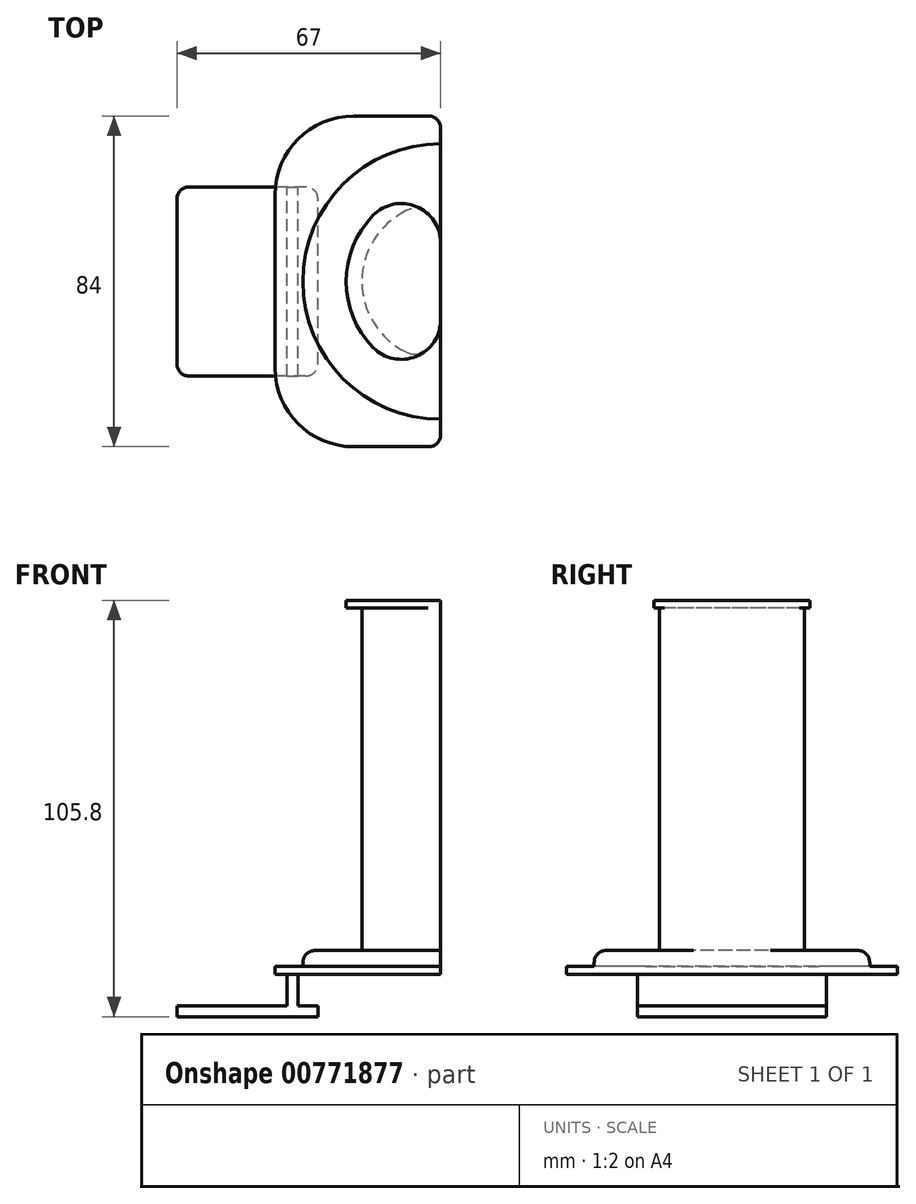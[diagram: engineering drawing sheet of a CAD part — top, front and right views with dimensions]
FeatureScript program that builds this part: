
annotation { "Feature Type Name" : "Feature", "Feature Type Description" : "" }
export const myFeature = defineFeature(function(context is Context, id is Id, definition is map)
    precondition{}
    {
        {
            var Q0;
            Q0=qCreatedBy(makeId("Top.planeOp"),FACE);
            var sketch = newSketch(context, id + "F0", { "sketchPlane" : qUnion([Q0])});
            skCircle(sketch, "E0", {"center": v(0, 0) * mm, "radius": 42 * mm});
            skCircle(sketch, "E1", {"center": v(0, 0) * mm, "radius": 35 * mm});
            skCircle(sketch, "E2", {"center": v(0, 0) * mm, "radius": 20 * mm});
            skLineSegment(sketch, "E3", {"start": v(0, -20) * mm, "end": v(0, 20) * mm});
            skLineSegment(sketch, "E4", {"start": v(0, -42) * mm, "end": v(0, 42) * mm});
            skLineSegment(sketch, "E5.bottom", {"start": v(-22.08, -42) * mm, "end": v(22.08, -42) * mm});
            skLineSegment(sketch, "E5.top", {"start": v(-22.08, 42) * mm, "end": v(22.08, 42) * mm});
            skLineSegment(sketch, "E5.left", {"start": v(-42.08, -22) * mm, "end": v(-42.08, 22) * mm});
            skLineSegment(sketch, "E5.right", {"start": v(42.08, -22) * mm, "end": v(42.08, 22) * mm});
            skPoint(sketch, "E6.visualSharp", {"position": v(-42.08, -42) * mm});
            skArc(sketch, "E6.filletArc", {"start": v(-42.08, -22) * mm, "mid": v(-36.23, -36.14) * mm, "end": v(-22.08, -42) * mm});
            skPoint(sketch, "E7.visualSharp", {"position": v(-42.08, 42) * mm});
            skArc(sketch, "E7.filletArc", {"start": v(-22.08, 42) * mm, "mid": v(-36.23, 36.14) * mm, "end": v(-42.08, 22) * mm});
            skPoint(sketch, "E8.visualSharp", {"position": v(42.08, -42) * mm});
            skArc(sketch, "E8.filletArc", {"start": v(22.08, -42) * mm, "mid": v(36.23, -36.14) * mm, "end": v(42.08, -22) * mm});
            skPoint(sketch, "E9.visualSharp", {"position": v(42.08, 42) * mm});
            skArc(sketch, "E9.filletArc", {"start": v(42.08, 22) * mm, "mid": v(36.23, 36.14) * mm, "end": v(22.08, 42) * mm});
            skSolve(sketch);
        }
        {
            var Q0;
            {var subQ0=sQuery(id+"F0.wireOp",EDGE,"E4");var subQ4=sQuery(id+"F0.wireOp",EDGE,"E1");var subQ6=makeQuery(id+"F0.imprint","INTERSECT",VERTEX,{"disambiguationData":[OD(0.0)],"derivedFrom":[subQ4,subQ0]});Q0=makeQuery(id+"F0.imprint","IMPRINT",FACE,{"disambiguationData":[TD([[makeQuery(id+"F0.imprint","IMPRINT",EDGE,{"disambiguationData":[TD([[subQ6,1.0]])],"derivedFrom":subQ4}),-1.0]])]});}
            var Q1;
            {var subQ0=sQuery(id+"F0.wireOp",EDGE,"E4");var subQ1=sQuery(id+"F0.wireOp",EDGE,"E2");var subQ2=makeQuery(id+"F0.imprint","INTERSECT",VERTEX,{"disambiguationData":[OD(0.0)],"derivedFrom":[subQ1,subQ0]});Q1=makeQuery(id+"F0.imprint","IMPRINT",FACE,{"disambiguationData":[TD([[makeQuery(id+"F0.imprint","IMPRINT",EDGE,{"disambiguationData":[TD([[subQ2,1.0]])],"derivedFrom":subQ1}),1.0]])]});}
            var Q2;
            {var subQ0=sQuery(id+"F0.wireOp",EDGE,"E4");var subQ1=sQuery(id+"F0.wireOp",EDGE,"E1");var subQ2=makeQuery(id+"F0.imprint","INTERSECT",VERTEX,{"disambiguationData":[OD(0.0)],"derivedFrom":[subQ1,subQ0]});Q2=makeQuery(id+"F0.imprint","IMPRINT",FACE,{"disambiguationData":[TD([[makeQuery(id+"F0.imprint","IMPRINT",EDGE,{"disambiguationData":[TD([[subQ2,1.0]])],"derivedFrom":subQ1}),1.0]])]});}
            var Q3;
            Q3=makeQuery(id+"F0.imprint","IMPRINT",FACE,{"disambiguationData":[TD([[makeQuery(id+"F0.imprint","IMPRINT",EDGE,{"derivedFrom":sQuery(id+"F0.wireOp",EDGE,"E5.left")}),-1.0]])]});
            extrude(context, id + "F1", {"entities" : qUnion([Q0, Q1, Q2, Q3]), "depth" : 2 * mm});
        }
        {
            var Q0;
            {var subQ0=sQuery(id+"F0.wireOp",EDGE,"E4");var subQ1=sQuery(id+"F0.wireOp",EDGE,"E1");var subQ2=makeQuery(id+"F0.imprint","INTERSECT",VERTEX,{"disambiguationData":[OD(0.0)],"derivedFrom":[subQ1,subQ0]});Q0=makeQuery(id+"F0.imprint","IMPRINT",FACE,{"disambiguationData":[TD([[makeQuery(id+"F0.imprint","IMPRINT",EDGE,{"disambiguationData":[TD([[subQ2,1.0]])],"derivedFrom":subQ1}),1.0]])]});}
            var Q1;
            {var subQ0=sQuery(id+"F0.wireOp",EDGE,"E4");var subQ1=sQuery(id+"F0.wireOp",EDGE,"E2");var subQ2=makeQuery(id+"F0.imprint","INTERSECT",VERTEX,{"disambiguationData":[OD(0.0)],"derivedFrom":[subQ1,subQ0]});Q1=makeQuery(id+"F0.imprint","IMPRINT",FACE,{"disambiguationData":[TD([[makeQuery(id+"F0.imprint","IMPRINT",EDGE,{"disambiguationData":[TD([[subQ2,1.0]])],"derivedFrom":subQ1}),1.0]])]});}
            extrude(context, id + "F2", {"entities" : qUnion([Q0, Q1]), "operationType" : NewBodyOperationType.ADD, "depth" : 6 * mm});
        }
        {
            var Q0;
            {var subQ0=sQuery(id+"F0.wireOp",EDGE,"E4");var subQ1=sQuery(id+"F0.wireOp",EDGE,"E2");var subQ2=makeQuery(id+"F0.imprint","INTERSECT",VERTEX,{"disambiguationData":[OD(0.0)],"derivedFrom":[subQ1,subQ0]});Q0=makeQuery(id+"F0.imprint","IMPRINT",FACE,{"disambiguationData":[TD([[makeQuery(id+"F0.imprint","IMPRINT",EDGE,{"disambiguationData":[TD([[subQ2,1.0]])],"derivedFrom":subQ1}),1.0]])]});}
            extrude(context, id + "F3", {"entities" : qUnion([Q0]), "operationType" : NewBodyOperationType.ADD, "depth" : 95 * mm, "offsetDistance" : 25 * mm});
        }
        {
            var Q0;
            Q0=makeQuery(id+"F3.opExtrude","CAP_FACE",FACE,{"disambiguationData":[OSD([sQuery(id+"F0.wireOp",EDGE,"E2")])],"isStart":false});
            var sketch = newSketch(context, id + "F4", { "sketchPlane" : qUnion([Q0])});
            skCircle(sketch, "E10", {"center": v(0, 0) * mm, "radius": 24 * mm});
            skLineSegment(sketch, "E11", {"start": v(0, 24) * mm, "end": v(0, -24) * mm});
            skSolve(sketch);
        }
        {
            var Q0;
            {var subQ0=sQuery(id+"F4.wireOp",EDGE,"E11");var subQ1=sQuery(id+"F4.wireOp",EDGE,"E10");var subQ2=makeQuery(id+"F4.imprint","INTERSECT",VERTEX,{"disambiguationData":[OD(0.0)],"derivedFrom":[subQ1,subQ0]});Q0=makeQuery(id+"F4.imprint","IMPRINT",FACE,{"disambiguationData":[TD([[makeQuery(id+"F4.imprint","IMPRINT",EDGE,{"disambiguationData":[TD([[subQ2,-1.0]])],"derivedFrom":subQ1}),1.0]])]});}
            extrude(context, id + "F5", {"entities" : qUnion([Q0]), "operationType" : NewBodyOperationType.ADD, "oppositeDirection" : true, "depth" : 2 * mm});
        }
        {
            var Q0;
            {var subQ0=sQuery(id+"F4.wireOp",EDGE,"E11");var subQ1=sQuery(id+"F4.wireOp",EDGE,"E10");Q0=makeQuery(id+"F5.opExtrude","SWEPT_EDGE",EDGE,{"disambiguationData":[OSD([subQ1,subQ0]),TDD([makeQuery(id+"F4.imprint","INTERSECT",VERTEX,{"disambiguationData":[OD(0.0)],"derivedFrom":[subQ1,subQ0]})])]});}
            var Q1;
            {var subQ0=sQuery(id+"F4.wireOp",EDGE,"E11");var subQ1=sQuery(id+"F4.wireOp",EDGE,"E10");Q1=makeQuery(id+"F5.opExtrude","SWEPT_EDGE",EDGE,{"disambiguationData":[OSD([subQ1,subQ0]),TDD([makeQuery(id+"F4.imprint","INTERSECT",VERTEX,{"disambiguationData":[OD(1.0)],"derivedFrom":[subQ1,subQ0]})])]});}
            fillet(context, id + "F6", {"entities" : qUnion([Q0, Q1]), "radius" : 10 * mm, "tangentPropagation" : true, "allowEdgeOverflow" : false});
        }
        {
            var Q0;
            {var subQ0=sQuery(id+"F0.wireOp",EDGE,"E4");var subQ1=sQuery(id+"F0.wireOp",EDGE,"E1");var subQ2=makeQuery(id+"F0.imprint","INTERSECT",VERTEX,{"disambiguationData":[OD(0.0)],"derivedFrom":[subQ1,subQ0]});Q0=makeQuery(id+"F0.imprint","IMPRINT",FACE,{"disambiguationData":[TD([[makeQuery(id+"F0.imprint","IMPRINT",EDGE,{"disambiguationData":[TD([[subQ2,1.0]])],"derivedFrom":subQ1}),1.0]])]});}
            var sketch = newSketch(context, id + "F7", { "sketchPlane" : qUnion([Q0])});
            skLineSegment(sketch, "E12.bottom", {"start": v(-39, -24) * mm, "end": v(-36.2, -24) * mm});
            skLineSegment(sketch, "E12.top", {"start": v(-39, 24) * mm, "end": v(-36.2, 24) * mm});
            skLineSegment(sketch, "E12.left", {"start": v(-39, -24) * mm, "end": v(-39, 24) * mm});
            skLineSegment(sketch, "E12.right", {"start": v(-36.2, -24) * mm, "end": v(-36.2, 24) * mm});
            skPoint(sketch, "E12.middle", {"position": v(-37.6, 0) * mm});
            skSolve(sketch);
        }
        {
            var Q0;
            Q0=makeQuery(id+"F7.imprint","IMPRINT",FACE,{"disambiguationData":[TD([[makeQuery(id+"F7.imprint","IMPRINT",EDGE,{"derivedFrom":sQuery(id+"F7.wireOp",EDGE,"E12.bottom")}),1.0]])]});
            extrude(context, id + "F8", {"entities" : qUnion([Q0]), "operationType" : NewBodyOperationType.ADD, "oppositeDirection" : true, "depth" : 8 * mm});
        }
        {
            var Q0;
            Q0=makeQuery(id+"F8.opExtrude","CAP_FACE",FACE,{"disambiguationData":[OSD([sQuery(id+"F7.wireOp",EDGE,"E12.bottom"),sQuery(id+"F7.wireOp",EDGE,"E12.top"),sQuery(id+"F7.wireOp",EDGE,"E12.left"),sQuery(id+"F7.wireOp",EDGE,"E12.right")])],"isStart":false});
            var sketch = newSketch(context, id + "F9", { "sketchPlane" : qUnion([Q0])});
            skLineSegment(sketch, "E13.bottom", {"start": v(-11, 24) * mm, "end": v(-67, 24) * mm});
            skLineSegment(sketch, "E13.top", {"start": v(-11, -24) * mm, "end": v(-67, -24) * mm});
            skLineSegment(sketch, "E13.left", {"start": v(-11, 24) * mm, "end": v(-11, -24) * mm});
            skLineSegment(sketch, "E13.right", {"start": v(-67, 24) * mm, "end": v(-67, -24) * mm});
            skPoint(sketch, "E13.middle", {"position": v(-39, 0) * mm});
            skLineSegment(sketch, "E14", {"start": v(-31.2, 24) * mm, "end": v(-31.2, -24) * mm});
            skSolve(sketch);
        }
        {
            var Q0;
            {var subQ2=sQuery(id+"F9.wireOp",EDGE,"E13.right");Q0=makeQuery(id+"F9.imprint","IMPRINT",FACE,{"disambiguationData":[TD([[makeQuery(id+"F9.imprint","IMPRINT",EDGE,{"derivedFrom":subQ2}),1.0]])]});}
            var Q1;
            {var subQ2=sQuery(id+"F9.wireOp",EDGE,"E14");Q1=makeQuery(id+"F9.imprint","IMPRINT",FACE,{"disambiguationData":[TD([[makeQuery(id+"F9.imprint","IMPRINT",EDGE,{"derivedFrom":subQ2}),-1.0]])]});}
            var Q2;
            {var subQ1=makeQuery(id+"F8.opExtrude","CAP_EDGE",EDGE,{"disambiguationData":[OSD([sQuery(id+"F7.wireOp",EDGE,"E12.left")])],"isStart":false});Q2=makeQuery(id+"F9.imprint","IMPRINT",FACE,{"disambiguationData":[TD([[makeQuery(id+"F9.imprint","IMPRINT",EDGE,{"derivedFrom":subQ1}),1.0]])]});}
            extrude(context, id + "F10", {"entities" : qUnion([Q0, Q1, Q2]), "operationType" : NewBodyOperationType.ADD, "depth" : 2.8 * mm});
        }
        {
            var Q0;
            Q0=makeQuery(id+"F10.opExtrude","SWEPT_EDGE",EDGE,{"disambiguationData":[OSD([sQuery(id+"F9.wireOp",EDGE,"E13.bottom"),sQuery(id+"F9.wireOp",EDGE,"E13.right")])]});
            var Q1;
            Q1=makeQuery(id+"F10.opExtrude","SWEPT_EDGE",EDGE,{"disambiguationData":[OSD([sQuery(id+"F9.wireOp",EDGE,"E13.bottom"),sQuery(id+"F9.wireOp",EDGE,"E14")])]});
            var Q2;
            Q2=makeQuery(id+"F10.opExtrude","SWEPT_EDGE",EDGE,{"disambiguationData":[OSD([sQuery(id+"F9.wireOp",EDGE,"E13.top"),sQuery(id+"F9.wireOp",EDGE,"E13.right")])]});
            var Q3;
            Q3=makeQuery(id+"F10.opExtrude","SWEPT_EDGE",EDGE,{"disambiguationData":[OSD([sQuery(id+"F9.wireOp",EDGE,"E13.top"),sQuery(id+"F9.wireOp",EDGE,"E14")])]});
            var Q4;
            Q4=makeQuery(id+"F1.opExtrude","SWEPT_EDGE",EDGE,{"disambiguationData":[OSD([sQuery(id+"F0.wireOp",EDGE,"E0"),sQuery(id+"F0.wireOp",EDGE,"E4"),sQuery(id+"F0.wireOp",EDGE,"E5.top")])]});
            var Q5;
            Q5=makeQuery(id+"F1.opExtrude","SWEPT_EDGE",EDGE,{"disambiguationData":[OSD([sQuery(id+"F0.wireOp",EDGE,"E0"),sQuery(id+"F0.wireOp",EDGE,"E4"),sQuery(id+"F0.wireOp",EDGE,"E5.bottom")])]});
            var Q6;
            Q6=makeQuery(id+"F2.opExtrude","CAP_EDGE",EDGE,{"disambiguationData":[OSD([sQuery(id+"F0.wireOp",EDGE,"E1")])],"isStart":false});
            fillet(context, id + "F11", {"entities" : qUnion([Q0, Q1, Q2, Q3, Q4, Q5, Q6]), "radius" : 3 * mm, "tangentPropagation" : true, "allowEdgeOverflow" : false});
        }
        {
            var Q0;
            {var subQ0=sQuery(id+"F4.wireOp",EDGE,"E11");var subQ1=sQuery(id+"F4.wireOp",EDGE,"E10");Q0=makeQuery(id+"F6.opFillet","BLEND_EDGE",EDGE,{"blendedFrom":[makeQuery(id+"F5.opExtrude","SWEPT_EDGE",EDGE,{"disambiguationData":[OSD([subQ1,subQ0]),TDD([makeQuery(id+"F4.imprint","INTERSECT",VERTEX,{"disambiguationData":[OD(1.0)],"derivedFrom":[subQ1,subQ0]})])]}),makeQuery(id+"F3.opExtrude","SWEPT_FACE",FACE,{"disambiguationData":[OSD([sQuery(id+"F0.wireOp",EDGE,"E2")])]})],"blendedInto":[makeQuery(id+"F3.opExtrude","SWEPT_FACE",FACE,{"disambiguationData":[OSD([sQuery(id+"F0.wireOp",EDGE,"E2")])]})]});}
            var Q1;
            {var subQ0=sQuery(id+"F4.wireOp",EDGE,"E11");var subQ1=sQuery(id+"F4.wireOp",EDGE,"E10");Q1=makeQuery(id+"F6.opFillet","BLEND_EDGE",EDGE,{"blendedFrom":[makeQuery(id+"F5.opExtrude","SWEPT_EDGE",EDGE,{"disambiguationData":[OSD([subQ1,subQ0]),TDD([makeQuery(id+"F4.imprint","INTERSECT",VERTEX,{"disambiguationData":[OD(0.0)],"derivedFrom":[subQ1,subQ0]})])]}),makeQuery(id+"F3.opExtrude","SWEPT_FACE",FACE,{"disambiguationData":[OSD([sQuery(id+"F0.wireOp",EDGE,"E2")])]})],"blendedInto":[makeQuery(id+"F3.opExtrude","SWEPT_FACE",FACE,{"disambiguationData":[OSD([sQuery(id+"F0.wireOp",EDGE,"E2")])]})]});}
            fillet(context, id + "F12", {"entities" : qUnion([Q0, Q1]), "radius" : 5 * mm, "tangentPropagation" : true, "allowEdgeOverflow" : false});
        }
    });
